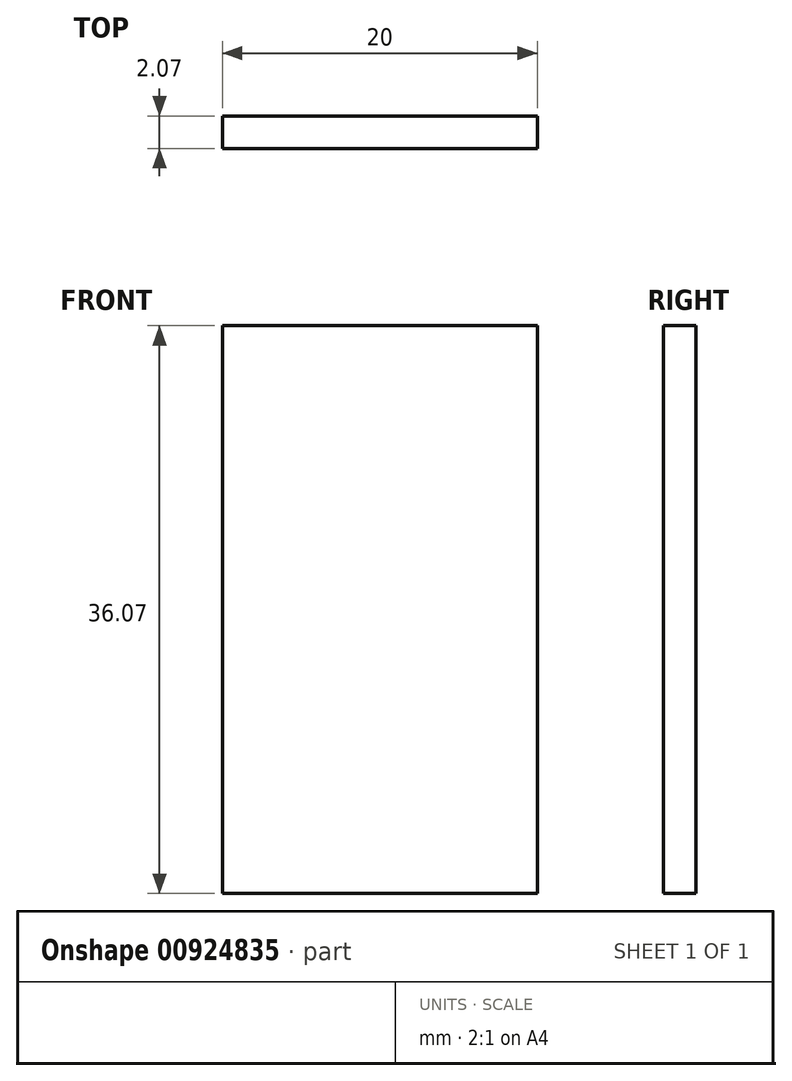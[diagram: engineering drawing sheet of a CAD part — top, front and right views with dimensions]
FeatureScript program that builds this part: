
annotation { "Feature Type Name" : "Feature", "Feature Type Description" : "" }
export const myFeature = defineFeature(function(context is Context, id is Id, definition is map)
    precondition{}
    {
        {
            var Q0;
            Q0=qCreatedBy(makeId("Top.planeOp"),FACE);
            var sketch = newSketch(context, id + "F0", { "sketchPlane" : qUnion([Q0])});
            skLineSegment(sketch, "E0.bottom", {"start": v(-10, -2.22) * mm, "end": v(10, -2.22) * mm});
            skLineSegment(sketch, "E0.top", {"start": v(-10, -0.15) * mm, "end": v(10, -0.15) * mm});
            skLineSegment(sketch, "E0.left", {"start": v(-10, -2.22) * mm, "end": v(-10, -0.15) * mm});
            skLineSegment(sketch, "E0.right", {"start": v(10, -2.22) * mm, "end": v(10, -0.15) * mm});
            skPoint(sketch, "E0.middle", {"position": v(0, -1.19) * mm});
            skLineSegment(sketch, "E1.bottom", {"start": v(-10, -2.22) * mm, "end": v(-10, -2.22) * mm});
            skLineSegment(sketch, "E1.top", {"start": v(-10, -18.37) * mm, "end": v(-10, -18.37) * mm});
            skLineSegment(sketch, "E1.left", {"start": v(-10, -2.22) * mm, "end": v(-10, -18.37) * mm});
            skLineSegment(sketch, "E1.right", {"start": v(-10, -2.22) * mm, "end": v(-10, -18.37) * mm});
            skLineSegment(sketch, "E2.bottom", {"start": v(10, -2.22) * mm, "end": v(10, -2.22) * mm});
            skLineSegment(sketch, "E2.top", {"start": v(10, -18.38) * mm, "end": v(10, -18.38) * mm});
            skLineSegment(sketch, "E2.left", {"start": v(10, -2.22) * mm, "end": v(10, -18.38) * mm});
            skLineSegment(sketch, "E2.right", {"start": v(10, -2.22) * mm, "end": v(10, -18.38) * mm});
            skSolve(sketch);
        }
        {
            var Q0;
            Q0=makeQuery(id+"F0.imprint","IMPRINT",FACE,{"disambiguationData":[TD([[makeQuery(id+"F0.imprint","IMPRINT",EDGE,{"derivedFrom":sQuery(id+"F0.wireOp",EDGE,"E0.bottom")}),1.0]])]});
            extrude(context, id + "F1", {"entities" : qUnion([Q0]), "depth" : 36.07 * mm, "offsetDistance" : 25.4 * mm});
        }
    });
